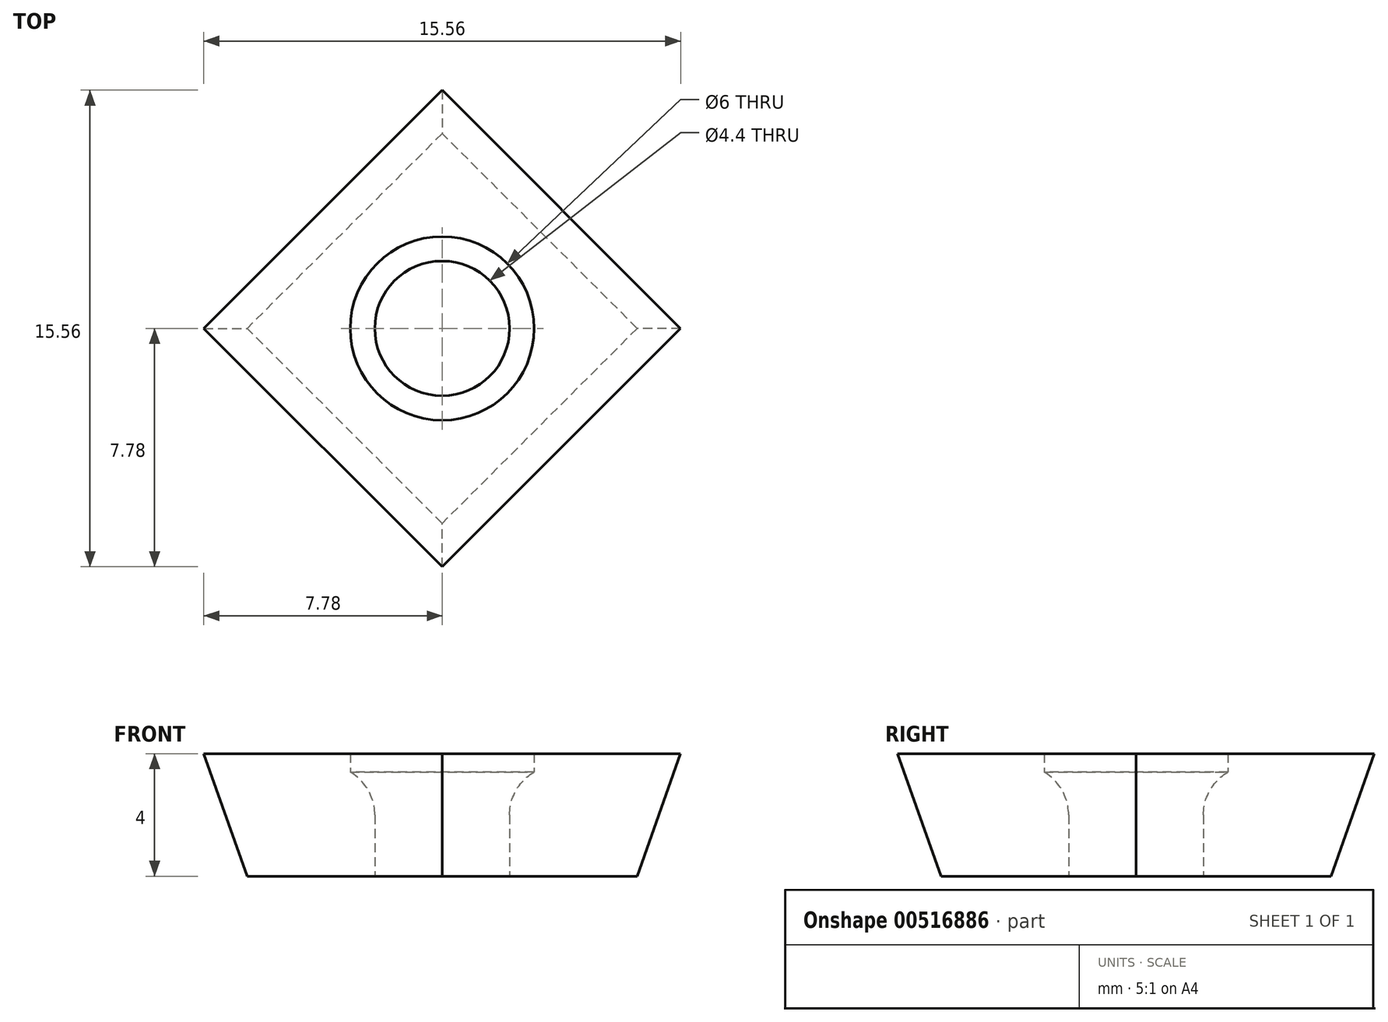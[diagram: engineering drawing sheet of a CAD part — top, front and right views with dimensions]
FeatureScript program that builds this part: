
annotation { "Feature Type Name" : "Feature", "Feature Type Description" : "" }
export const myFeature = defineFeature(function(context is Context, id is Id, definition is map)
    precondition{}
    {
        {
            var Q0;
            Q0=qCreatedBy(makeId("Top.planeOp"),FACE);
            var sketch = newSketch(context, id + "F0", { "sketchPlane" : qUnion([Q0])});
            skLineSegment(sketch, "E0.bottom", {"start": v(5.5, 5.5) * mm, "end": v(-5.5, 5.5) * mm});
            skLineSegment(sketch, "E0.top", {"start": v(5.5, -5.5) * mm, "end": v(-5.5, -5.5) * mm});
            skLineSegment(sketch, "E0.left", {"start": v(5.5, 5.5) * mm, "end": v(5.5, -5.5) * mm});
            skLineSegment(sketch, "E0.right", {"start": v(-5.5, 5.5) * mm, "end": v(-5.5, -5.5) * mm});
            skPoint(sketch, "E0.middle", {"position": v(0, 0) * mm});
            skSolve(sketch);
        }
        {
            var Q0;
            Q0=qCreatedBy(makeId("Top.planeOp"),FACE);
            cPlane(context, id + "F1", {"entities" : qUnion([Q0]), "cplaneType" : CPlaneType.OFFSET, "offset" : 4 * mm, "oppositeDirection" : true, "width" : 150 * mm, "height" : 150 * mm});
        }
        {
            var Q0;
            Q0=qCreatedBy(id+"F1.planeOp",FACE);
            var sketch = newSketch(context, id + "F2", { "sketchPlane" : qUnion([Q0])});
            skLineSegment(sketch, "E1.bottom", {"start": v(4.5, 4.5) * mm, "end": v(-4.5, 4.5) * mm});
            skLineSegment(sketch, "E1.top", {"start": v(4.5, -4.5) * mm, "end": v(-4.5, -4.5) * mm});
            skLineSegment(sketch, "E1.left", {"start": v(4.5, 4.5) * mm, "end": v(4.5, -4.5) * mm});
            skLineSegment(sketch, "E1.right", {"start": v(-4.5, 4.5) * mm, "end": v(-4.5, -4.5) * mm});
            skPoint(sketch, "E1.middle", {"position": v(0, 0) * mm});
            skSolve(sketch);
        }
        {
            var Q0;
            Q0=makeQuery(id+"F0.imprint","IMPRINT",FACE,{"disambiguationData":[TD([[makeQuery(id+"F0.imprint","IMPRINT",EDGE,{"derivedFrom":sQuery(id+"F0.wireOp",EDGE,"E0.bottom")}),1.0]])]});
            var Q1;
            Q1=makeQuery(id+"F2.imprint","IMPRINT",FACE,{"disambiguationData":[TD([[makeQuery(id+"F2.imprint","IMPRINT",EDGE,{"derivedFrom":sQuery(id+"F2.wireOp",EDGE,"E1.bottom")}),1.0]])]});
            loft(context, id + "F3", {"sheetProfilesArray" : [{ "sheetProfileEntities" : qUnion([Q0]) }, { "sheetProfileEntities" : qUnion([Q1]) }]});
        }
        {
            var Q0;
            Q0=qCreatedBy(makeId("Front.planeOp"),FACE);
            var sketch = newSketch(context, id + "F4", { "sketchPlane" : qUnion([Q0])});
            skLineSegment(sketch, "E2", {"start": v(0, 0.97) * mm, "end": v(0, -4.96) * mm, "construction": true});
            skLineSegment(sketch, "E3.0", {"start": v(4.5, -4) * mm, "end": v(0, -4) * mm});
            skLineSegment(sketch, "E4.0", {"start": v(5.5, 0) * mm, "end": v(0, 0) * mm});
            skLineSegment(sketch, "E5", {"start": v(2.2, -4) * mm, "end": v(2.2, -2) * mm});
            skLineSegment(sketch, "E6", {"start": v(3, 0) * mm, "end": v(3, -0.6) * mm});
            skArc(sketch, "E7", {"start": v(2.2, -2) * mm, "mid": v(2.41, -1.2) * mm, "end": v(3, -0.6) * mm});
            skLineSegment(sketch, "E8", {"start": v(0, 0) * mm, "end": v(0, -4) * mm});
            skPoint(sketch, "E9.orphan", {"position": v(-5.5, 0) * mm});
            skPoint(sketch, "E10.orphan", {"position": v(-4.5, -4) * mm});
            skSolve(sketch);
        }
        {
            var Q0;
            Q0 = qSketchRegion(id + "F4", true);
            var Q1;
            Q1=sQuery(id+"F4.wireOp",EDGE,"E2");
            revolve(context, id + "F5", {"operationType" : NewBodyOperationType.REMOVE, "entities" : qUnion([Q0]), "axis" : qUnion([Q1]), "revolveType" : RevolveType.FULL, "oppositeDirection" : true});
        }
        {
            var Q0;
            Q0=makeQuery(id+"F3.opLoft","SWEPT_BODY",BODY,{"disambiguationData":[OSD([makeQuery(id+"F0.imprint","IMPRINT",FACE,{"disambiguationData":[TD([[makeQuery(id+"F0.imprint","IMPRINT",EDGE,{"derivedFrom":sQuery(id+"F0.wireOp",EDGE,"E0.bottom")}),1.0]])]}),makeQuery(id+"F2.imprint","IMPRINT",FACE,{"disambiguationData":[TD([[makeQuery(id+"F2.imprint","IMPRINT",EDGE,{"derivedFrom":sQuery(id+"F2.wireOp",EDGE,"E1.bottom")}),1.0]])]})])]});
            var Q1;
            Q1=sQuery(id+"F4.wireOp",EDGE,"E8");
            transform(context, id + "F6", {"entities" : qUnion([Q0]), "transformType" : TransformType.ROTATION, "transformAxis" : qUnion([Q1]), "angle" : 45 * degree, "makeCopy" : false});
        }
    });
